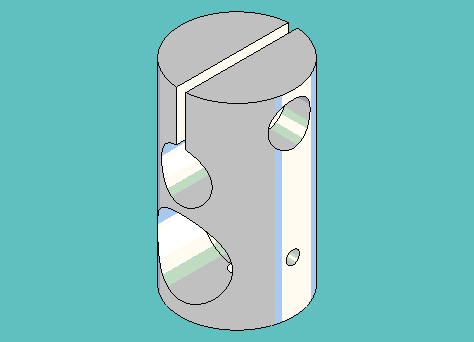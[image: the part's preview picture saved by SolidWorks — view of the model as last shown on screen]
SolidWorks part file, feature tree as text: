
SOLIDWORKS PART (.sldprt)
format: sldprt  version: not decoded by parser v0  size: 948,736 bytes
history: native  units: mm
features: sketch x10, extrude x5, boolean_combine x5, cut_extrude x3, revolve x2, plane x2, material x1 (+11 scaffold rows collapsed)
feature tree (39):
  scaffold x11  (default folders/planes/origin — collapsed)
  material  "Material <not specified>"
  sketch  "Sketch1"  dims[D1=33.3375mm D2=9.525mm D3=153.9875mm]
  revolve  "Revolve1"  Angle=360deg
  sketch  "Sketch2"  dims[c1.D1=3.4544mm c1.D2=2.159mm c1.D3=8.7376mm c1.D4=28.3464mm c2.D3=8.7376mm c2.D4=28.3464mm]
  extrude  "Extrude1"  [1 undecoded]
  boolean_combine  "Combine1"
  sketch  "Sketch3"  dims[D1=2.159mm]
  extrude  "Extrude2"  Depth=7.9756mm
  sketch  "Sketch5"  dims[c1.D4=~4.437453mm c1.D5=6.35mm c1.D1=8.7376mm c1.D2=6.35mm c1.D3=6.35mm c2.D4=9.525mm c2.D2=9.525mm c3.D4=9.525mm c3.D6=12.7mm c4.D4=10.16mm]
  revolve  "Revolve2"  Angle=360deg
  boolean_combine  "Combine4"
  sketch  "Sketch11"  dims[D1=~10.31875mm]
  cut_extrude  "Cut-Extrude1"  Depth=177.8mm
  boolean_combine  "Combine5"
  sketch  "Sketch6"  dims[D1=8.5852mm D2=20.6502mm]
  extrude  "Extrude3"  [1 undecoded]
  boolean_combine  "Combine6"
  sketch  "Sketch9"  dims[c1.D1=4.3688mm c1.D2=2.2606mm c1.D3=8.7376mm c1.D4=28.3464mm c2.D3=8.7376mm c2.D4=28.3464mm]
  extrude  "Extrude5"  [1 undecoded]
  plane  "Plane1"  Offset=12.7mm
  sketch  "Sketch10"  dims[D1=~7.14375mm]
  extrude  "Extrude6"  Depth=7.9375mm
  boolean_combine  "Combine7"
  sketch  "Sketch13"  dims[D1=~0.79375mm D2=~0.79375mm]
  cut_extrude  "Cut-Extrude2"  Depth=12.7mm
  sketch  "Sketch14"  dims[D1=6.35mm]
  cut_extrude  "Cut-Extrude3"  [1 undecoded]
  plane  "Plane2"  Offset=0.79375mm
decode coverage: 16 of 25 modeling features carry decoded parameters
note: ~ marks probable driven/reference dimensions
note: 4 parameter values undecoded
summary: no parameter record found for 4 features
note: suppression state not decoded; provenance and decode notes live in map.json
